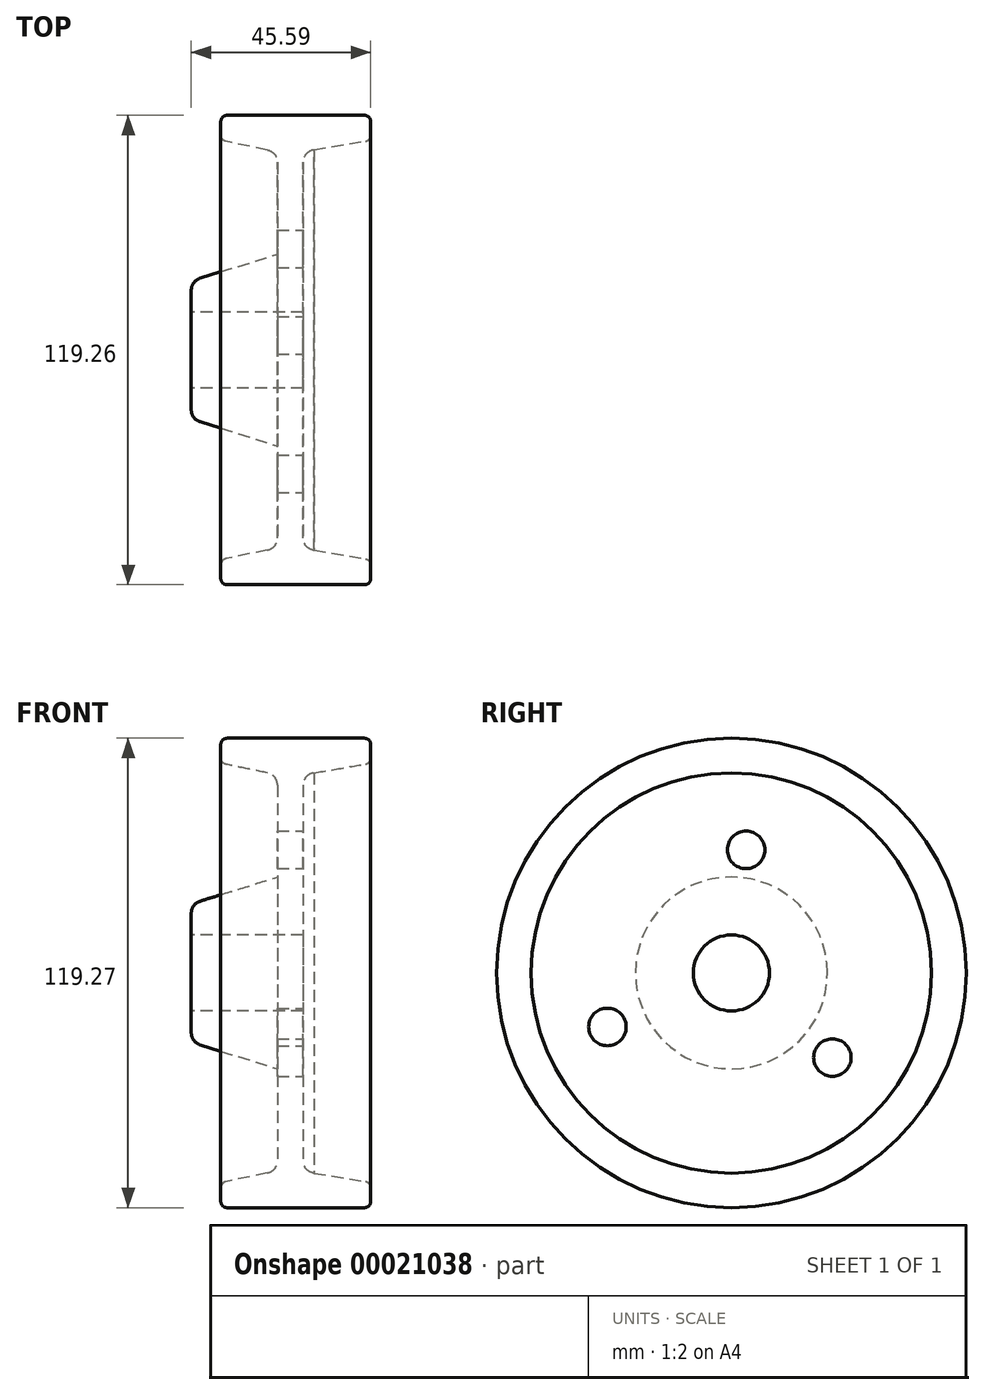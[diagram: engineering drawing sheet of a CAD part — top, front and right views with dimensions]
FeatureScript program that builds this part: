
annotation { "Feature Type Name" : "Feature", "Feature Type Description" : "" }
export const myFeature = defineFeature(function(context is Context, id is Id, definition is map)
    precondition{}
    {
        {
            var Q0;
            Q0=qCreatedBy(makeId("Front.planeOp"),FACE);
            var sketch = newSketch(context, id + "F0", { "sketchPlane" : qUnion([Q0])});
            skLineSegment(sketch, "E0", {"start": v(-12.47, 9.78) * mm, "end": v(25.63, 9.78) * mm});
            skLineSegment(sketch, "E1", {"start": v(25.63, 9.78) * mm, "end": v(25.63, 16.13) * mm});
            skLineSegment(sketch, "E2", {"start": v(-12.47, 9.78) * mm, "end": v(-12.47, 16.13) * mm});
            skLineSegment(sketch, "E3", {"start": v(-12.47, 16.13) * mm, "end": v(-0.6, 18.6) * mm});
            skLineSegment(sketch, "E4", {"start": v(25.63, 16.13) * mm, "end": v(10.93, 18.6) * mm});
            skLineSegment(sketch, "E5", {"start": v(1.93, 21.7) * mm, "end": v(1.93, 59.76) * mm});
            skLineSegment(sketch, "E6", {"start": v(8.28, 21.72) * mm, "end": v(8.28, 59.76) * mm});
            skPoint(sketch, "E7.visualSharp", {"position": v(1.93, 19.12) * mm});
            skArc(sketch, "E7.filletArc", {"start": v(-0.6, 18.6) * mm, "mid": v(1.22, 19.7) * mm, "end": v(1.93, 21.7) * mm});
            skPoint(sketch, "E8.visualSharp", {"position": v(8.28, 19.03) * mm});
            skArc(sketch, "E8.filletArc", {"start": v(8.28, 21.72) * mm, "mid": v(9.03, 19.67) * mm, "end": v(10.93, 18.6) * mm});
            skLineSegment(sketch, "E9", {"start": v(-19.96, 59.76) * mm, "end": v(-19.96, 54.22) * mm});
            skLineSegment(sketch, "E10", {"start": v(-19.97, 59.76) * mm, "end": v(30.83, 59.76) * mm});
            skLineSegment(sketch, "E11", {"start": v(-17.74, 51.2) * mm, "end": v(1.93, 45.04) * mm});
            skPoint(sketch, "E12.visualSharp", {"position": v(-19.96, 51.89) * mm});
            skArc(sketch, "E12.filletArc", {"start": v(-19.96, 54.22) * mm, "mid": v(-19.35, 52.34) * mm, "end": v(-17.74, 51.2) * mm});
            skLineSegment(sketch, "E13", {"start": v(-19.96, 69.42) * mm, "end": v(30.84, 69.42) * mm});
            skLineSegment(sketch, "E14", {"start": v(5.19, 9.78) * mm, "end": v(5.19, 59.76) * mm});
            skArc(sketch, "E15.MirrorCS", {"start": v(30.34, 54.22) * mm, "mid": v(29.72, 52.34) * mm, "end": v(28.11, 51.2) * mm});
            skArc(sketch, "E16.MirrorCS", {"start": v(10.97, 18.6) * mm, "mid": v(9.16, 19.7) * mm, "end": v(8.44, 21.7) * mm});
            skLineSegment(sketch, "E17.MirrorCS", {"start": v(22.84, 9.78) * mm, "end": v(22.84, 16.13) * mm});
            skPoint(sketch, "E18.MirrorP", {"position": v(8.44, 19.12) * mm});
            skPoint(sketch, "E19.MirrorP", {"position": v(30.34, 51.89) * mm});
            skLineSegment(sketch, "E20.MirrorCS", {"start": v(30.34, 59.76) * mm, "end": v(30.34, 54.22) * mm});
            skLineSegment(sketch, "E21.MirrorCS", {"start": v(22.84, 16.13) * mm, "end": v(10.97, 18.6) * mm});
            skLineSegment(sketch, "E22.MirrorCS", {"start": v(8.44, 21.7) * mm, "end": v(8.44, 59.76) * mm});
            skLineSegment(sketch, "E23.MirrorCS", {"start": v(28.11, 51.2) * mm, "end": v(8.44, 45.04) * mm});
            skLineSegment(sketch, "E24.MirrorCS", {"start": v(22.84, 9.78) * mm, "end": v(-15.26, 9.78) * mm});
            skLineSegment(sketch, "E25.MirrorCS", {"start": v(30.34, 59.76) * mm, "end": v(-20.46, 59.76) * mm});
            skSolve(sketch);
        }
        {
            var Q0;
            Q0=makeQuery(id+"F0.imprint","IMPRINT",FACE,{"disambiguationData":[TD([[makeQuery(id+"F0.imprint","IMPRINT",EDGE,{"derivedFrom":sQuery(id+"F0.wireOp",EDGE,"E0")}),1.0]])]});
            var Q1;
            {var subQ1=sQuery(id+"F0.wireOp",EDGE,"E9");Q1=makeQuery(id+"F0.imprint","IMPRINT",FACE,{"disambiguationData":[TD([[makeQuery(id+"F0.imprint","IMPRINT",EDGE,{"derivedFrom":subQ1}),1.0]])]});}
            var Q2;
            Q2=makeQuery(id+"F0.imprint","IMPRINT",FACE,{"disambiguationData":[TD([[makeQuery(id+"F0.imprint","IMPRINT",EDGE,{"derivedFrom":sQuery(id+"F0.wireOp",EDGE,"E15.MirrorCS")}),-1.0]])]});
            var Q3;
            {var subQ2=sQuery(id+"F0.wireOp",EDGE,"E6");Q3=makeQuery(id+"F0.imprint","IMPRINT",FACE,{"disambiguationData":[TD([[makeQuery(id+"F0.imprint","IMPRINT",EDGE,{"derivedFrom":subQ2}),1.0]])]});}
            var Q4;
            {var subQ5=sQuery(id+"F0.wireOp",EDGE,"E2");Q4=makeQuery(id+"F0.imprint","IMPRINT",FACE,{"disambiguationData":[TD([[makeQuery(id+"F0.imprint","IMPRINT",EDGE,{"derivedFrom":subQ5}),-1.0]])]});}
            var Q5;
            {var subQ3=sQuery(id+"F0.wireOp",EDGE,"E6");Q5=makeQuery(id+"F0.imprint","IMPRINT",FACE,{"disambiguationData":[TD([[makeQuery(id+"F0.imprint","IMPRINT",EDGE,{"derivedFrom":subQ3}),-1.0]])]});}
            var Q6;
            Q6=sQuery(id+"F0.wireOp",EDGE,"E13");
            revolve(context, id + "F1", {"entities" : qUnion([Q0, Q1, Q2, Q3, Q4, Q5]), "axis" : qUnion([Q6]), "revolveType" : RevolveType.FULL});
        }
        {
            var Q0;
            Q0=makeQuery(id+"F1.opRevolve","SWEPT_FACE",FACE,{"disambiguationData":[OSD([sQuery(id+"F0.wireOp",EDGE,"E22.MirrorCS")])]});
            var sketch = newSketch(context, id + "F2", { "sketchPlane" : qUnion([Q0])});
            skCircle(sketch, "E26", {"center": v(-31.5, 55.7) * mm, "radius": 4.76 * mm});
            skCircle(sketch, "E27", {"center": v(25.65, 47.9) * mm, "radius": 4.76 * mm});
            skCircle(sketch, "E28", {"center": v(3.74, 100.69) * mm, "radius": 4.76 * mm});
            skSolve(sketch);
        }
        {
            var Q0;
            Q0=makeQuery(id+"F2.imprint","IMPRINT",FACE,{"disambiguationData":[TD([[makeQuery(id+"F2.imprint","IMPRINT",EDGE,{"derivedFrom":sQuery(id+"F2.wireOp",EDGE,"E28")}),1.0]])]});
            var Q1;
            Q1=makeQuery(id+"F2.imprint","IMPRINT",FACE,{"disambiguationData":[TD([[makeQuery(id+"F2.imprint","IMPRINT",EDGE,{"derivedFrom":sQuery(id+"F2.wireOp",EDGE,"E26")}),1.0]])]});
            var Q2;
            Q2=makeQuery(id+"F2.imprint","IMPRINT",FACE,{"disambiguationData":[TD([[makeQuery(id+"F2.imprint","IMPRINT",EDGE,{"derivedFrom":sQuery(id+"F2.wireOp",EDGE,"E27")}),1.0]])]});
            var Q3;
            Q3=sQuery(id+"F2.wireOp",EDGE,"E28");
            var Q4;
            Q4=sQuery(id+"F2.wireOp",EDGE,"E27");
            var Q5;
            Q5=sQuery(id+"F2.wireOp",EDGE,"E26");
            extrude(context, id + "F3", {"entities" : qUnion([Q0, Q1, Q2]), "operationType" : NewBodyOperationType.REMOVE, "surfaceEntities" : qUnion([Q3, Q4, Q5]), "oppositeDirection" : true, "depth" : 25.4 * mm});
        }
        {
            var Q0;
            Q0=makeQuery(id+"F1.opRevolve","SWEPT_FACE",FACE,{"disambiguationData":[OSD([sQuery(id+"F0.wireOp",EDGE,"E1")])]});
            var Q1;
            Q1=makeQuery(id+"F1.opRevolve","SWEPT_EDGE",EDGE,{"disambiguationData":[OSD([sQuery(id+"F0.wireOp",EDGE,"E1"),sQuery(id+"F0.wireOp",EDGE,"E4")])]});
            fillet(context, id + "F4", {"entities" : qUnion([Q0, Q1]), "radius" : 1.59 * mm, "tangentPropagation" : true, "allowEdgeOverflow" : false});
        }
        {
            var Q0;
            Q0=makeQuery(id+"F1.opRevolve","SWEPT_EDGE",EDGE,{"disambiguationData":[OSD([sQuery(id+"F0.wireOp",EDGE,"E2"),sQuery(id+"F0.wireOp",EDGE,"E24.MirrorCS")])]});
            var Q1;
            Q1=makeQuery(id+"F1.opRevolve","SWEPT_EDGE",EDGE,{"disambiguationData":[OSD([sQuery(id+"F0.wireOp",EDGE,"E2"),sQuery(id+"F0.wireOp",EDGE,"E3")])]});
            fillet(context, id + "F5", {"entities" : qUnion([Q0, Q1]), "radius" : 1.59 * mm, "tangentPropagation" : true, "allowEdgeOverflow" : false});
        }
    });
